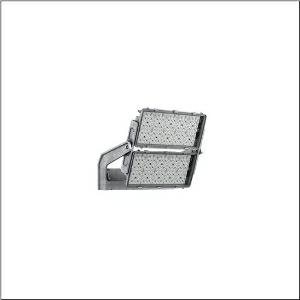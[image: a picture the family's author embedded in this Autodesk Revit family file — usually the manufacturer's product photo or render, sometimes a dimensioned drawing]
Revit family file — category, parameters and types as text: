
# Revit family: floodlight_fl_11_maxi___rs07_5xa779117k01ba_0df9
name_source: partatom
category: Lighting Fixtures
units: mm (PartAtom-declared; Revit-internal decimal feet)

## family parameters
Cut with Voids When Loaded = No
Host = Face
Light Source = No
Part Type = Normal
Room Calculation Point = No
Round Connector Dimension = Use Diameter
Shared = No

## types (1)
- --- (1 x LED, 104100 lm, 757.5 W, 5000K)
    Apparent Load = 757 VA
    CIE Flux Codes = 80 93 99 100 99
    Color Rendering = 70
    Color Temperature = 5000K
    Default Elevation = 1800 mm
    Description = Floodlight FL 11  maxi floodlight; light control with lens of PMMA; cover panel of toughened safety glass, transparent; light distribution: RS07, asymmetric direct distribution, LEDcolour temperature: 5000K, rated luminous flux: 104.100lm, colour rendering: CRI > 70, light colour: 750; luminous efficacy: 137lm/W; with terminal, 8-pole, max. 2.5mm², mains connection: 220..240V/380..400V AC, 50/60Hz, surge voltage resistance: line to ground: 10kV, LED unit replaceable, LED unit replaceable without ESD environment, dimming range 0.1..100%; 758W floodlight LED unit of diecast aluminium, coated grey; length: 713mm / width: 651mm / height: 338mm; housing frame, of diecast aluminium, uncoated, natural, mounting bracket, of diecast aluminium, equipment: Power, protection rating (complete): IP66; insulation class (complete): insulation class I (protective earthing); certification: CE, ENEC, VDE; ball protection: ball impact resistance with accessories, permissible storage temperature: -40..+85°C; packaging unit: 1 piece

Light Distribution: RS07
    Height = 320 mm
    Lamp = 1 x LED
    Lamp Light Flux = 104100 lm
    Lamp Power = 757.5 W
    Lamp count = 1
    Length = 712 mm
    Luminous efficacy = 137 lm/W
    Manufacturer = Siteco
    ModVariant = No
    Model = 5XA779117K01BA
    Number of Poles = 1
    OnlyDefault = Yes
    Power Factor = 1
    Product Name = Floodlight FL 11 maxi | RS07
    Product group = floodlight | pylon top
    ProductGroupID = 6101
    Protection Class = Protection class I
    Protection Degree = IP 66
    RLX_Detail_Level = 1
    RlxData = <blob elided: 41837 chars, md5=e7508905>
    Socket = socket
    Standby Power = 0 W
    System Light Flux = 104100 lm
    System Power = 757 W
    Type Comments = factory setting: luminous flux: 100 % | dim-lin: 254 | 790 mA
    Type Image = l_1006932.jpg
    URL = http://relux.com
    VarID = @adj_001349
    Voltage = 0 V
    Weight = 0.00 kg
    Width = 655 mm

## geometry (parser evidence)
native form markers: Blend x4, Sweep x12
no freeform markers — native parametric forms only
